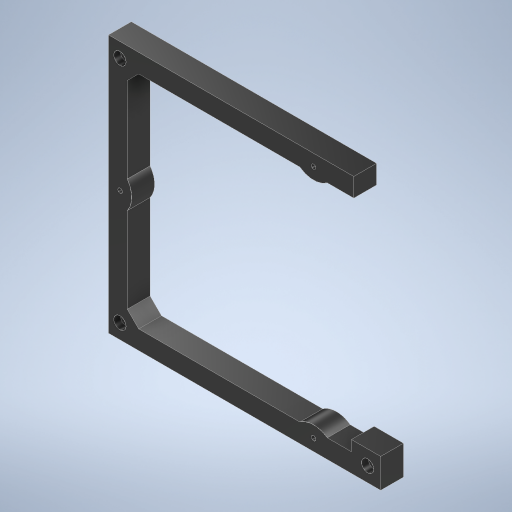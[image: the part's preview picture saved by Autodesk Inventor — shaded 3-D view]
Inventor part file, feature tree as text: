
AUTODESK INVENTOR PART (.ipt)
format: ipt  version: 2024.3 (Build 283343000, 343)  size: 329,216 bytes
history: native  units: mm
features: projected_geometry x4, hole x3, extrude x2, other x1, chamfer x1
ambient origin geometry x8: Origin, YZ Plane, XZ Plane, XY Plane, X Axis, Y Axis, Z Axis, Center Point
bodies: Body1 (feature_tree)
feature tree (11):
  other  "Těleso1"
  extrude  "Vysunutí1"  Depth=11.5mm
  chamfer  "Zkosení1"  Distance=11.5mm
  extrude  "Vysunutí2"  Depth=11.5mm
  hole  "Díra1"  [1 undecoded]
  hole  "Díra2"  [1 undecoded]
  hole  "Díra3"  [1 undecoded]
  projected_geometry  "Promítnutá smyčka1"
  projected_geometry  "Promítnutá smyčka2"
  projected_geometry  "Promítnutá smyčka3"
  projected_geometry  "Promítnutá smyčka4"
note: 3 required parameter values undecoded (feature->parameter linkage not recoverable at this tier; creation-order binding heuristic only, values carry confidence <= 0.55)
